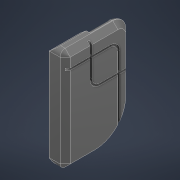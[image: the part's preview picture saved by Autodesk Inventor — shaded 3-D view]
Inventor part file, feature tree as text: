
AUTODESK INVENTOR PART (.ipt)
format: ipt  version: 2022.1 (Build 261234000, 234)  size: 378,368 bytes
history: native  units: mm
features: delete_face x14, direct_edit x5, fillet x5, move_body x5, sketch x4, extrude x3, chamfer x3, projected_geometry x2, hole x1, other x1
ambient origin geometry x8: Origin, YZ Plane, XZ Plane, XY Plane, X Axis, Y Axis, Z Axis, Center Point
bodies: Volumenkörper1 (feature_tree)
feature tree (43):
  delete_face  "Fläche löschen1"
  delete_face  "Fläche löschen2"
  delete_face  "Fläche löschen3"
  delete_face  "Fläche löschen4"
  delete_face  "Fläche löschen5"
  delete_face  "Fläche löschen6"
  delete_face  "Fläche löschen7"
  delete_face  "Fläche löschen8"
  delete_face  "Fläche löschen9"
  extrude  "Extrusion1"  Depth=10.0mm
  delete_face  "Fläche löschen10"
  sketch  "Skizze2"  dims[d3=11.464466mm]
  delete_face  "Fläche löschen11"
  delete_face  "Fläche löschen12"
  hole  "Bohrung1"  [1 undecoded]
  direct_edit  "Direktbearbeitung1"
  delete_face  "Fläche löschen13"
  direct_edit  "Direktbearbeitung2"
  direct_edit  "Direktbearbeitung3"
  direct_edit  "Direktbearbeitung4"
  direct_edit  "Direktbearbeitung5"
  extrude  "Extrusion2"  TaperAngle=0.0deg  [1 undecoded]
  chamfer  "Fase1"  [1 undecoded]
  delete_face  "Fläche löschen14"
  fillet  "Rundung1"  Radius=17.0mm
  chamfer  "Fase2"  [1 undecoded]
  fillet  "Rundung2"  Radius=2.4mm
  fillet  "Rundung3"  Radius=5.0mm
  fillet  "Rundung4"  Radius=2.4mm
  chamfer  "Fase3"  Distance=2.0mm
  fillet  "Rundung5"  Radius=2.0mm
  extrude  "Extrusion3"  Depth=3.0mm
  sketch  "Skizze1"  dims[d0=10.0mm d1=0.0mm d2=17.0mm]
  projected_geometry  "Projizierte Kontur1"
  sketch  "Skizze3"  dims[d4=6.08mm d5=6.0mm d6=5.9mm d7=1.12mm d8=90.0deg d9=3.0mm d10=0.0mm d11=0.0mm d12=0.0mm d13=-0.5mm]
  projected_geometry  "Projizierte Kontur2"
  sketch  "Skizze4"  dims[d14=0.0mm d15=0.0mm d16=-1.5mm d17=0.0mm d18=0.0mm d19=-0.6mm d20=0.0mm d21=0.0mm d22=-0.2mm d23=0.0mm d24=0.0mm d25=17.0mm d26=0.0mm d27=0.0mm d28=2.4mm d29=2.0mm d30=45.0deg d31=5.0mm d32=2.4mm d33=2.0mm d34=45.0deg d35=2.0mm d36=2.0mm d37=14.0mm d38=2.0mm d39=2.0mm d40=45.0deg d41=1.6mm d42=0.8mm d43=0.8mm d44=5.0mm d45=5.0mm d46=0.8mm d47=0.8mm d48=5.0mm d49=5.0mm d50=3.0mm d51=3.8mm d52=1.0mm d53=0.0mm]
  other  "handle_b_x2"
  move_body  "Verschieben1"
  move_body  "Verschieben2"
  move_body  "Verschieben3"
  move_body  "Verschieben4"
  move_body  "Verschieben5"
note: 4 required parameter values undecoded (feature->parameter linkage not recoverable at this tier; creation-order binding heuristic only, values carry confidence <= 0.55)
